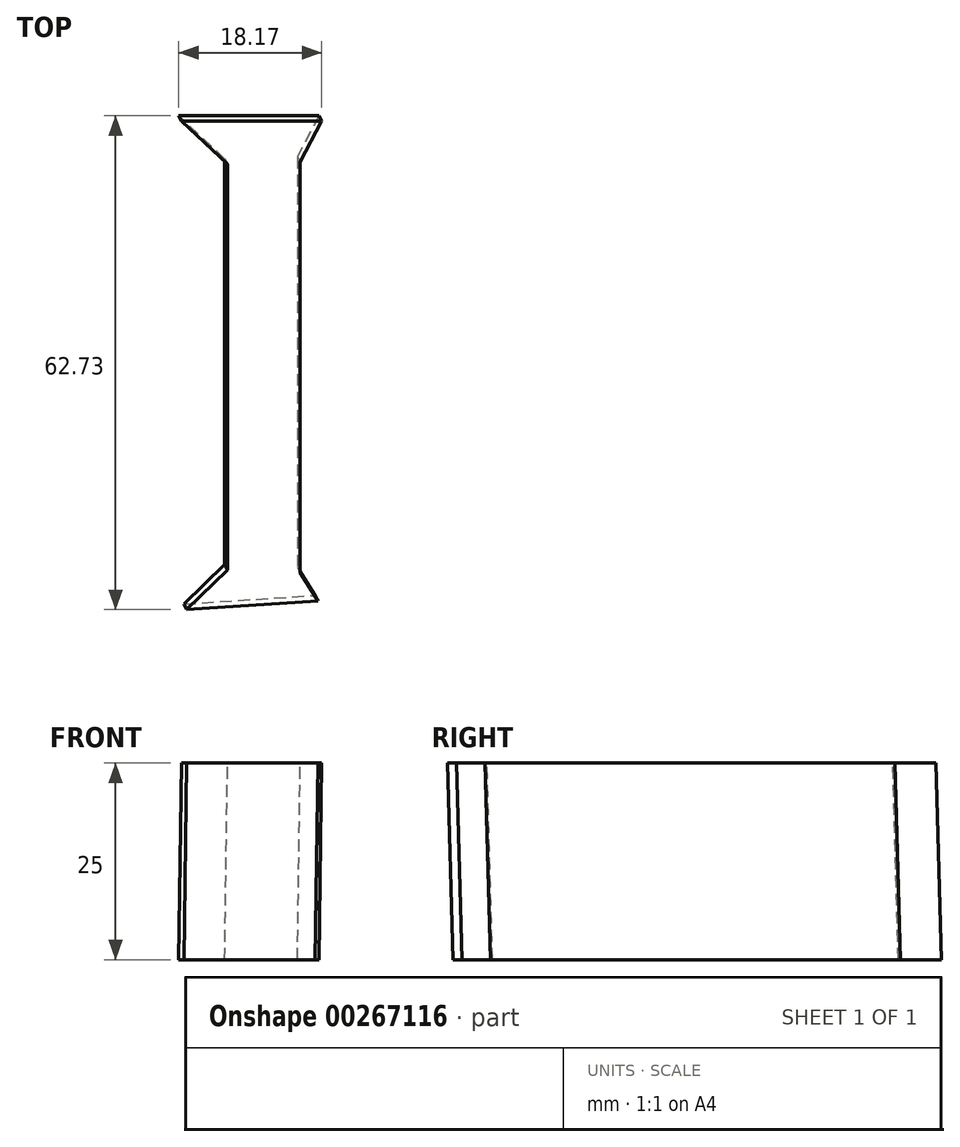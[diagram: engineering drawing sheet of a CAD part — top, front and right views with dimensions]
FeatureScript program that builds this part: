
annotation { "Feature Type Name" : "Feature", "Feature Type Description" : "" }
export const myFeature = defineFeature(function(context is Context, id is Id, definition is map)
    precondition{}
    {
        {
            var Q0;
            Q0=qCreatedBy(makeId("Top.planeOp"),FACE);
            var sketch = newSketch(context, id + "F0", { "sketchPlane" : qUnion([Q0])});
            skLineSegment(sketch, "E0", {"start": v(-11.5, 7.02) * mm, "end": v(-17.35, 12.5) * mm});
            skLineSegment(sketch, "E1", {"start": v(-17.35, 12.5) * mm, "end": v(0.46, 12.5) * mm});
            skLineSegment(sketch, "E2", {"start": v(0.46, 12.5) * mm, "end": v(-2.27, 7.31) * mm});
            skLineSegment(sketch, "E3", {"start": v(-11.5, 7.02) * mm, "end": v(-11.5, -44.52) * mm});
            skLineSegment(sketch, "E4", {"start": v(-2.27, 7.31) * mm, "end": v(-2.27, -44.8) * mm});
            skLineSegment(sketch, "E5", {"start": v(-2.27, -44.8) * mm, "end": v(0, -48.42) * mm});
            skLineSegment(sketch, "E6", {"start": v(-11.5, -44.52) * mm, "end": v(-16.7, -49.53) * mm});
            skLineSegment(sketch, "E7", {"start": v(-16.7, -49.53) * mm, "end": v(0, -48.42) * mm});
            skSolve(sketch);
        }
        {
            var Q0;
            Q0=qCreatedBy(makeId("Top.planeOp"),FACE);
            cPlane(context, id + "F1", {"entities" : qUnion([Q0]), "cplaneType" : CPlaneType.OFFSET, "offset" : 25 * mm, "width" : 150 * mm, "height" : 150 * mm});
        }
        {
            var Q0;
            Q0=qCreatedBy(id+"F1.planeOp",FACE);
            var sketch = newSketch(context, id + "F2", { "sketchPlane" : qUnion([Q0])});
            skLineSegment(sketch, "E8", {"start": v(-11.14, 6.33) * mm, "end": v(-16.99, 11.81) * mm});
            skLineSegment(sketch, "E9", {"start": v(-16.99, 11.81) * mm, "end": v(0.82, 11.81) * mm});
            skLineSegment(sketch, "E10", {"start": v(0.82, 11.81) * mm, "end": v(-1.9, 6.62) * mm});
            skLineSegment(sketch, "E11", {"start": v(-11.14, 6.33) * mm, "end": v(-11.14, -45.22) * mm});
            skLineSegment(sketch, "E12", {"start": v(-1.9, 6.62) * mm, "end": v(-1.9, -45.5) * mm});
            skLineSegment(sketch, "E13", {"start": v(-1.9, -45.5) * mm, "end": v(0.36, -49.11) * mm});
            skLineSegment(sketch, "E14", {"start": v(-11.14, -45.22) * mm, "end": v(-16.33, -50.22) * mm});
            skLineSegment(sketch, "E15", {"start": v(-16.33, -50.22) * mm, "end": v(0.36, -49.11) * mm});
            skSolve(sketch);
        }
        {
            var Q0;
            Q0=makeQuery(id+"F0.imprint","IMPRINT",FACE,{"disambiguationData":[TD([[makeQuery(id+"F0.imprint","IMPRINT",EDGE,{"derivedFrom":sQuery(id+"F0.wireOp",EDGE,"E0")}),-1.0]])]});
            var Q1;
            Q1=makeQuery(id+"F2.imprint","IMPRINT",FACE,{"disambiguationData":[TD([[makeQuery(id+"F2.imprint","IMPRINT",EDGE,{"derivedFrom":sQuery(id+"F2.wireOp",EDGE,"E8")}),-1.0]])]});
            loft(context, id + "F3", {"sheetProfilesArray" : [{ "sheetProfileEntities" : qUnion([Q0]) }, { "sheetProfileEntities" : qUnion([Q1]) }]});
        }
    });
